# Revit family: CITO 1x MW 1x 0°fH
name_source: partatom
category: HLS-Bauteile
units: mm (PartAtom-declared; Revit-internal decimal feet)

## family parameters
Arbeitsebenenbasiert = Nein
Beim Laden mit Abzugskörper schneiden = Nein
Bemaßung runder Anschluss = Durchmesser verwenden
Beschriftungsausrichtung beibehalten = Nein
Gemeinsam genutzt = Nein
Immer vertikal = Ja
Klassifizierung = Keine
Raumberechnungspunkt = Nein
Teiletyp = Normal

## types (21) — shared parameters
Anschluss Höhe = 40 mm  [stored 0.131234 ft]
Datenblatt = https://www.burkhalter-h2o.ch
Homepage = https://www.burkhalter-h2o.ch
zero-valued in all types: Vorgabe-Ansicht

## per-type parameters (varying)
| type | Anschluss Durchmesser | Anschluss Radius | DN | E | H | H1 | Harzinhalt | LUT | M | V | Verteilergrösse | Y |
| DN32 - 15L | 32 mm  [stored 0.104987 ft] | 14 mm  [stored 0.0459318 ft] | 32 mm  [stored 0.104987 ft] | 110 mm  [stored 0.360892 ft] | 1630 mm  [stored 5.34777 ft] | 780 mm  [stored 2.55906 ft] | 15L | LUT_CITO_DN32 | 130 mm  [stored 0.426509 ft] | 340 mm  [stored 1.11549 ft] | CITO 1x MW 1x 0°fH - DN32 : DN32 | 350 mm  [stored 1.14829 ft] |
| DN32 - 25L | 32 mm  [stored 0.104987 ft] | 14 mm  [stored 0.0459318 ft] | 32 mm  [stored 0.104987 ft] | 110 mm  [stored 0.360892 ft] | 1630 mm  [stored 5.34777 ft] | 780 mm  [stored 2.55906 ft] | 25L | LUT_CITO_DN32 | 130 mm  [stored 0.426509 ft] | 340 mm  [stored 1.11549 ft] | CITO 1x MW 1x 0°fH - DN32 : DN32 | 350 mm  [stored 1.14829 ft] |
| DN32 - 50L | 32 mm  [stored 0.104987 ft] | 14 mm  [stored 0.0459318 ft] | 32 mm  [stored 0.104987 ft] | 110 mm  [stored 0.360892 ft] | 1410 mm  [stored 4.62598 ft] | 560 mm  [stored 1.83727 ft] | 50L | LUT_CITO_DN32 | 130 mm  [stored 0.426509 ft] | 340 mm  [stored 1.11549 ft] | CITO 1x MW 1x 0°fH - DN32 : DN32 | 350 mm  [stored 1.14829 ft] |
| DN32 - 75L | 32 mm  [stored 0.104987 ft] | 14 mm  [stored 0.0459318 ft] | 32 mm  [stored 0.104987 ft] | 110 mm  [stored 0.360892 ft] | 1850 mm  [stored 6.06955 ft] | 1000 mm  [stored 3.28084 ft] | 75L | LUT_CITO_DN32 | 130 mm  [stored 0.426509 ft] | 340 mm  [stored 1.11549 ft] | CITO 1x MW 1x 0°fH - DN32 : DN32 | 350 mm  [stored 1.14829 ft] |
| DN32 - 100L | 32 mm  [stored 0.104987 ft] | 14 mm  [stored 0.0459318 ft] | 32 mm  [stored 0.104987 ft] | 110 mm  [stored 0.360892 ft] | 1850 mm  [stored 6.06955 ft] | 1000 mm  [stored 3.28084 ft] | 100L | LUT_CITO_DN32 | 130 mm  [stored 0.426509 ft] | 340 mm  [stored 1.11549 ft] | CITO 1x MW 1x 0°fH - DN32 : DN32 | 350 mm  [stored 1.14829 ft] |
| DN32 - 150L | 32 mm  [stored 0.104987 ft] | 14 mm  [stored 0.0459318 ft] | 32 mm  [stored 0.104987 ft] | 110 mm  [stored 0.360892 ft] | 1810 mm  [stored 5.93832 ft] | 960 mm  [stored 3.14961 ft] | 150L | LUT_CITO_DN32 | 130 mm  [stored 0.426509 ft] | 340 mm  [stored 1.11549 ft] | CITO 1x MW 1x 0°fH - DN32 : DN32 | 350 mm  [stored 1.14829 ft] |
| DN32 - 200L | 32 mm  [stored 0.104987 ft] | 14 mm  [stored 0.0459318 ft] | 32 mm  [stored 0.104987 ft] | 110 mm  [stored 0.360892 ft] | 1810 mm  [stored 5.93832 ft] | 960 mm  [stored 3.14961 ft] | 200L | LUT_CITO_DN32 | 130 mm  [stored 0.426509 ft] | 340 mm  [stored 1.11549 ft] | CITO 1x MW 1x 0°fH - DN32 : DN32 | 350 mm  [stored 1.14829 ft] |
| DN32 - 125L | 32 mm  [stored 0.104987 ft] | 14 mm  [stored 0.0459318 ft] | 32 mm  [stored 0.104987 ft] | 110 mm  [stored 0.360892 ft] | 1850 mm  [stored 6.06955 ft] | 1000 mm  [stored 3.28084 ft] | 125L | LUT_CITO_DN32 | 130 mm  [stored 0.426509 ft] | 340 mm  [stored 1.11549 ft] | CITO 1x MW 1x 0°fH - DN32 : DN32 | 350 mm  [stored 1.14829 ft] |
| DN40 - 50L | 40 mm  [stored 0.131234 ft] | 18 mm  [stored 0.0590551 ft] | 40 mm  [stored 0.131234 ft] | 120 mm  [stored 0.393701 ft] | 1420 mm | 480 mm  [stored 1.5748 ft] | 50L | LUT_CITO_DN40 | 140 mm  [stored 0.459318 ft] | 430 mm | CITO 1x MW 1x 0°fH - DN40 : DN40 | 500 mm  [stored 1.64042 ft] |
| DN40 - 75L | 40 mm  [stored 0.131234 ft] | 18 mm  [stored 0.0590551 ft] | 40 mm  [stored 0.131234 ft] | 120 mm  [stored 0.393701 ft] | 1870 mm  [stored 6.13517 ft] | 930 mm  [stored 3.05118 ft] | 75L | LUT_CITO_DN40 | 140 mm  [stored 0.459318 ft] | 430 mm | CITO 1x MW 1x 0°fH - DN40 : DN40 | 500 mm  [stored 1.64042 ft] |
| DN40 - 100L | 40 mm  [stored 0.131234 ft] | 18 mm  [stored 0.0590551 ft] | 40 mm  [stored 0.131234 ft] | 120 mm  [stored 0.393701 ft] | 1870 mm  [stored 6.13517 ft] | 930 mm  [stored 3.05118 ft] | 100L | LUT_CITO_DN40 | 140 mm  [stored 0.459318 ft] | 430 mm | CITO 1x MW 1x 0°fH - DN40 : DN40 | 500 mm  [stored 1.64042 ft] |
| DN40 - 125L | 40 mm  [stored 0.131234 ft] | 18 mm  [stored 0.0590551 ft] | 40 mm  [stored 0.131234 ft] | 120 mm  [stored 0.393701 ft] | 1870 mm  [stored 6.13517 ft] | 930 mm  [stored 3.05118 ft] | 125L | LUT_CITO_DN40 | 140 mm  [stored 0.459318 ft] | 430 mm | CITO 1x MW 1x 0°fH - DN40 : DN40 | 500 mm  [stored 1.64042 ft] |
| DN40 - 150L | 40 mm  [stored 0.131234 ft] | 18 mm  [stored 0.0590551 ft] | 40 mm  [stored 0.131234 ft] | 120 mm  [stored 0.393701 ft] | 1830 mm  [stored 6.00394 ft] | 890 mm  [stored 2.91995 ft] | 150L | LUT_CITO_DN40 | 140 mm  [stored 0.459318 ft] | 430 mm | CITO 1x MW 1x 0°fH - DN40 : DN40 | 500 mm  [stored 1.64042 ft] |
| DN40 - 200L | 40 mm  [stored 0.131234 ft] | 18 mm  [stored 0.0590551 ft] | 40 mm  [stored 0.131234 ft] | 120 mm  [stored 0.393701 ft] | 1830 mm  [stored 6.00394 ft] | 890 mm  [stored 2.91995 ft] | 200L | LUT_CITO_DN40 | 140 mm  [stored 0.459318 ft] | 430 mm | CITO 1x MW 1x 0°fH - DN40 : DN40 | 500 mm  [stored 1.64042 ft] |
| DN50 - 100L | 50 mm  [stored 0.164042 ft] | 23 mm  [stored 0.0754593 ft] | 50 mm  [stored 0.164042 ft] | 140 mm  [stored 0.459318 ft] | 1895 mm | 765 mm  [stored 2.50984 ft] | 100L | LUT_CITO_DN50 | 170 mm  [stored 0.557743 ft] | 450 mm  [stored 1.47638 ft] | CITO 1x MW 1x 0°fH - DN50 : DN50 | 500 mm  [stored 1.64042 ft] |
| DN50 - 125L | 50 mm  [stored 0.164042 ft] | 23 mm  [stored 0.0754593 ft] | 50 mm  [stored 0.164042 ft] | 140 mm  [stored 0.459318 ft] | 1895 mm | 765 mm  [stored 2.50984 ft] | 125L | LUT_CITO_DN50 | 170 mm  [stored 0.557743 ft] | 450 mm  [stored 1.47638 ft] | CITO 1x MW 1x 0°fH - DN50 : DN50 | 500 mm  [stored 1.64042 ft] |
| DN50 - 150L | 50 mm  [stored 0.164042 ft] | 23 mm  [stored 0.0754593 ft] | 50 mm  [stored 0.164042 ft] | 140 mm  [stored 0.459318 ft] | 1870 mm  [stored 6.13517 ft] | 740 mm  [stored 2.42782 ft] | 150L | LUT_CITO_DN50 | 170 mm  [stored 0.557743 ft] | 450 mm  [stored 1.47638 ft] | CITO 1x MW 1x 0°fH - DN50 : DN50 | 500 mm  [stored 1.64042 ft] |
| DN50 - 200L | 50 mm  [stored 0.164042 ft] | 23 mm  [stored 0.0754593 ft] | 50 mm  [stored 0.164042 ft] | 140 mm  [stored 0.459318 ft] | 1870 mm  [stored 6.13517 ft] | 740 mm  [stored 2.42782 ft] | 200L | LUT_CITO_DN50 | 170 mm  [stored 0.557743 ft] | 450 mm  [stored 1.47638 ft] | CITO 1x MW 1x 0°fH - DN50 : DN50 | 500 mm  [stored 1.64042 ft] |
| DN50 - 250L | 50 mm  [stored 0.164042 ft] | 23 mm  [stored 0.0754593 ft] | 50 mm  [stored 0.164042 ft] | 140 mm  [stored 0.459318 ft] | 2090 mm  [stored 6.85696 ft] | 960 mm  [stored 3.14961 ft] | 250L | LUT_CITO_DN50 | 170 mm  [stored 0.557743 ft] | 450 mm  [stored 1.47638 ft] | CITO 1x MW 1x 0°fH - DN50 : DN50 | 580 mm  [stored 1.90289 ft] |
| DN50 - 300L | 50 mm  [stored 0.164042 ft] | 23 mm  [stored 0.0754593 ft] | 50 mm  [stored 0.164042 ft] | 140 mm  [stored 0.459318 ft] | 2090 mm  [stored 6.85696 ft] | 960 mm  [stored 3.14961 ft] | 300L | LUT_CITO_DN50 | 170 mm  [stored 0.557743 ft] | 450 mm  [stored 1.47638 ft] | CITO 1x MW 1x 0°fH - DN50 : DN50 | 580 mm  [stored 1.90289 ft] |
| DN50 - 400L | 50 mm  [stored 0.164042 ft] | 23 mm  [stored 0.0754593 ft] | 50 mm  [stored 0.164042 ft] | 140 mm  [stored 0.459318 ft] | 2250 mm  [stored 7.38189 ft] | 1120 mm  [stored 3.67454 ft] | 400L | LUT_CITO_DN50 | 170 mm  [stored 0.557743 ft] | 450 mm  [stored 1.47638 ft] | CITO 1x MW 1x 0°fH - DN50 : DN50 | 580 mm  [stored 1.90289 ft] |

note: [stored X ft] marks values corroborated as IEEE doubles in the binary element streams (Revit-internal decimal feet)
